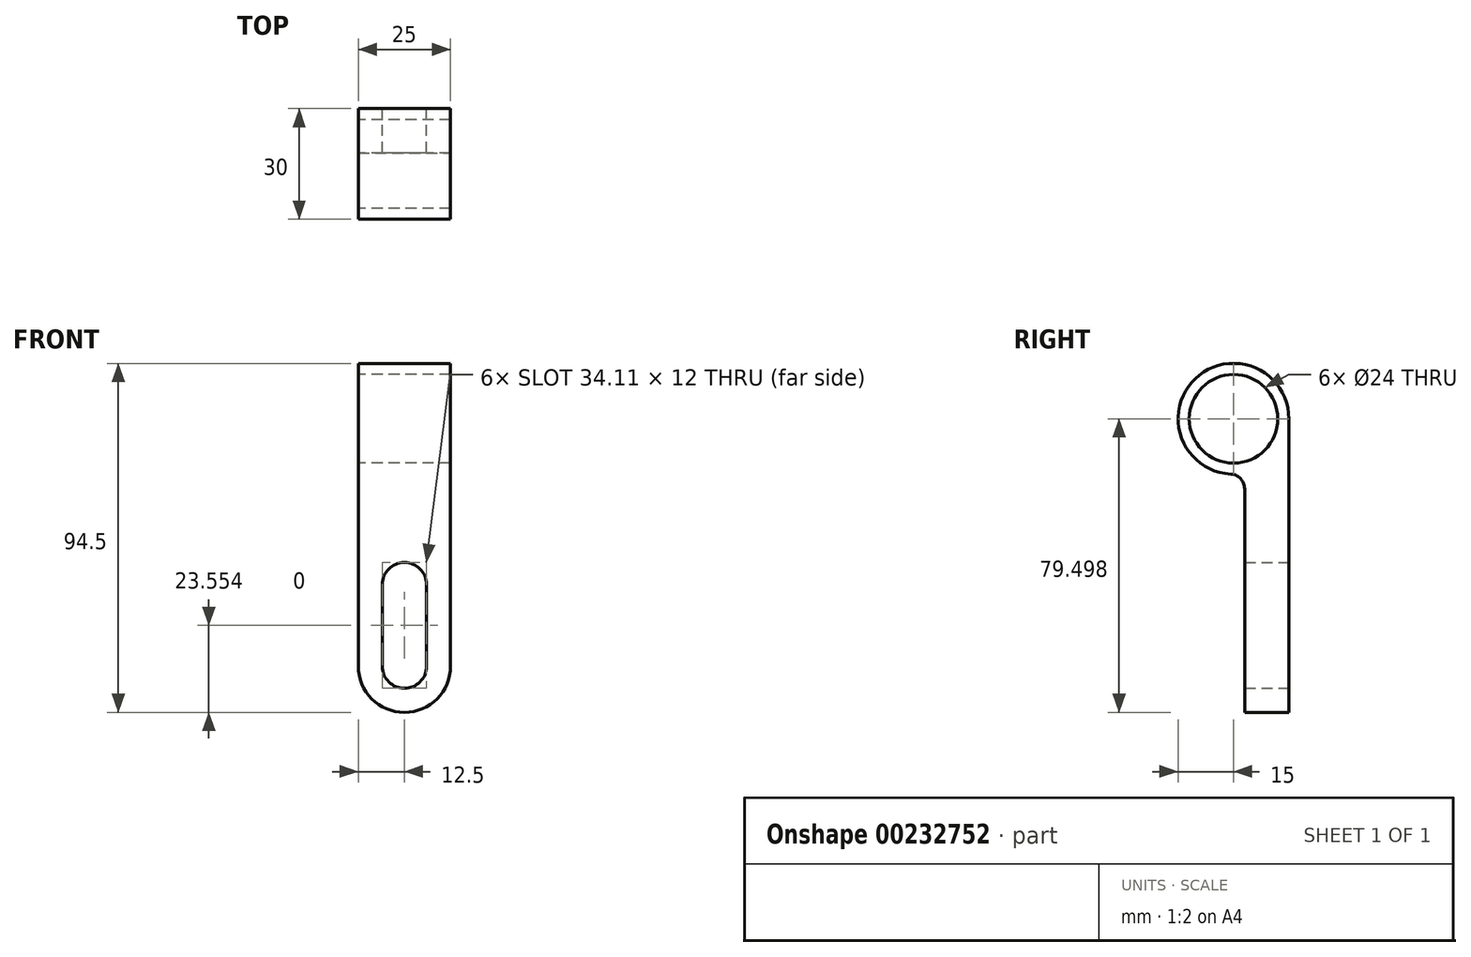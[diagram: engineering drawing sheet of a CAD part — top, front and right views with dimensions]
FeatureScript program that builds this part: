
annotation { "Feature Type Name" : "Feature", "Feature Type Description" : "" }
export const myFeature = defineFeature(function(context is Context, id is Id, definition is map)
    precondition{}
    {
        {
            var Q0;
            Q0=qCreatedBy(makeId("Right.planeOp"),FACE);
            var sketch = newSketch(context, id + "F0", { "sketchPlane" : qUnion([Q0])});
            skCircle(sketch, "E0", {"center": v(0, 25.76) * mm, "radius": 12 * mm});
            skArc(sketch, "E1", {"start": v(15, 25.76) * mm, "mid": v(-10.32, 36.64) * mm, "end": v(-0.79, 10.78) * mm});
            skLineSegment(sketch, "E2", {"start": v(15, 25.76) * mm, "end": v(15, -53.74) * mm});
            skLineSegment(sketch, "E3", {"start": v(15, -53.74) * mm, "end": v(3, -53.74) * mm});
            skLineSegment(sketch, "E4", {"start": v(3, -53.74) * mm, "end": v(3, 6.78) * mm});
            skPoint(sketch, "E5.visualSharp", {"position": v(3, 11.06) * mm});
            skArc(sketch, "E5.filletArc", {"start": v(3, 6.78) * mm, "mid": v(1.9, 9.54) * mm, "end": v(-0.79, 10.78) * mm});
            skSolve(sketch);
        }
        {
            var Q0;
            Q0 = qSketchRegion(id + "F0", true);
            extrude(context, id + "F1", {"entities" : qUnion([Q0]), "depth" : 25 * mm});
        }
        {
            var Q0;
            Q0=makeQuery(id+"F1.opExtrude","SWEPT_FACE",FACE,{"disambiguationData":[OSD([sQuery(id+"F0.wireOp",EDGE,"E2")])]});
            var sketch = newSketch(context, id + "F2", { "sketchPlane" : qUnion([Q0])});
            skLineSegment(sketch, "E6", {"start": v(-25, 23.6) * mm, "end": v(-25, -41.24) * mm, "construction": true});
            skLineSegment(sketch, "E7", {"start": v(0, 25.76) * mm, "end": v(0, -41.24) * mm});
            skArc(sketch, "E8", {"start": v(-25, -41.24) * mm, "mid": v(-12.5, -53.74) * mm, "end": v(0, -41.24) * mm});
            skArc(sketch, "E9", {"start": v(-6.5, -19.13) * mm, "mid": v(-12.5, -13.13) * mm, "end": v(-18.5, -19.13) * mm});
            skArc(sketch, "E10", {"start": v(-18.5, -41.24) * mm, "mid": v(-12.5, -47.24) * mm, "end": v(-6.5, -41.24) * mm});
            skLineSegment(sketch, "E11", {"start": v(-18.5, -41.24) * mm, "end": v(-18.5, -19.13) * mm});
            skLineSegment(sketch, "E12", {"start": v(-6.5, -41.24) * mm, "end": v(-6.5, -19.13) * mm});
            skSolve(sketch);
        }
        {
            var Q0;
            {var subQ0=sQuery(id+"F2.wireOp",EDGE,"E8");var subQ1=sQuery(id+"F0.wireOp",EDGE,"E2");var subQ2=makeQuery(id+"F1.opExtrude","CAP_EDGE",EDGE,{"disambiguationData":[OSD([subQ1])],"isStart":true});var subQ3=makeQuery(id+"F2.imprint","INTERSECT",VERTEX,{"derivedFrom":[subQ2,sQuery(id+"F2.wireOp",EDGE,"E7"),subQ0]});Q0=makeQuery(id+"F2.imprint","IMPRINT",FACE,{"disambiguationData":[TD([[makeQuery(id+"F2.imprint","IMPRINT",EDGE,{"disambiguationData":[TD([[subQ3,1.0]])],"derivedFrom":subQ0}),-1.0]])]});}
            var Q1;
            {var subQ0=sQuery(id+"F2.wireOp",EDGE,"E8");var subQ1=sQuery(id+"F0.wireOp",EDGE,"E2");var subQ2=makeQuery(id+"F1.opExtrude","CAP_EDGE",EDGE,{"disambiguationData":[OSD([subQ1])],"isStart":false});var subQ3=makeQuery(id+"F2.imprint","INTERSECT",VERTEX,{"derivedFrom":[subQ2,subQ0]});Q1=makeQuery(id+"F2.imprint","IMPRINT",FACE,{"disambiguationData":[TD([[makeQuery(id+"F2.imprint","IMPRINT",EDGE,{"disambiguationData":[TD([[subQ3,-1.0]])],"derivedFrom":subQ0}),-1.0]])]});}
            var Q2;
            Q2=makeQuery(id+"F2.imprint","IMPRINT",FACE,{"disambiguationData":[TD([[makeQuery(id+"F2.imprint","IMPRINT",EDGE,{"derivedFrom":sQuery(id+"F2.wireOp",EDGE,"E9")}),1.0]])]});
            extrude(context, id + "F3", {"entities" : qUnion([Q0, Q1, Q2]), "operationType" : NewBodyOperationType.REMOVE, "oppositeDirection" : true, "depth" : 25 * mm});
        }
    });
